# Revit family: 3039987 Lighting Fixture_Sylvania_Lumina Wave LED_Wall Mounted
name_source: partatom
category: Lighting Fixtures
revit_build: Autodesk Revit 2017 (Build: 20190507_1515(x64)
units: mm (PartAtom-declared; Revit-internal decimal feet)

## family parameters
Cut with Voids When Loaded = No
Host = Face
Light Source = Yes
OmniClass Number = 23.80.70.11.17
OmniClass Title = Specialized Lighting by Location or Use
Part Type = Normal
Room Calculation Point = No
Round Connector Dimension = Use Diameter
Shared = No

## types (1)
- Lumina Wave LED 2700K
    Accessory Material = Aluminum_Sylvania_Wave LED_White_RAL 9016
    Apparent Load = 6 VA
    Assembly Code = D5020200
    Body Material = Aluminum_Sylvania_Wave LED_White_RAL 9016
    Color Filter = 16777215
    Default Elevation = 0 mm  [stored 0 ft]
    Description = Lumina LED is a new range of ambient &
decorative LED wall lights. Consisting of
multiple decorative styles, they are suitable
for use in any hospitality or residential
application such as reception areas, hallways
and lounge spaces.
Lumina LED offers a selection of different
styles to suit multiple applications. With a
2,700K colour temperature it provides a soft
and ambient lighting effect.
Lumina LED provides direct/indirect ambient
light with an efficacy of up to 87lm/W; up to
50% more energy efficient than equivalent
products using traditional lamp sources.
    Dimming Lamp Color Temperature Shift = <None>
    Drive Current = 500mA
    Electrical Protection = Class II
    Emit Shape Visible in Rendering = No
    Emit from Circle Diameter = 5.3 mm  [stored 0.0173885 ft]
    Energy Class = A++, A+, A
    Height = 76 mm  [stored 0.249344 ft]
    IP Rating = IP20
    Lamp = LED
    Length = 254 mm  [stored 0.833333 ft]
    Life = 30 000h
    Light Distribution = Direct / Indirect
    Manufacturer = Feilo Sylvania
    Model = 3039987 Lumina Wave LED 2700K
    Mounting Length = 115 mm  [stored 0.377297 ft]
    Mounting Width = 50 mm  [stored 0.164042 ft]
    Photometric Web File = 3039987_LuminaWaveLED2700K-183091.ies
    Product Family = Lumina LED
    Product Page URL = http://www.sylvania-lighting.com
    Tilt Angle = -90.00°
    URL = http://www.sylvania-lighting.com
    Voltage = 240 V
    Voltage Comments = UNV (Universal Voltage; 100-240 Volt)
    Width = 64 mm  [stored 0.209974 ft]

note: [stored X ft] marks values corroborated as IEEE doubles in the binary element streams (Revit-internal decimal feet)

## geometry (parser evidence)
native form markers: Blend x2, Sweep x2
no freeform markers — native parametric forms only
